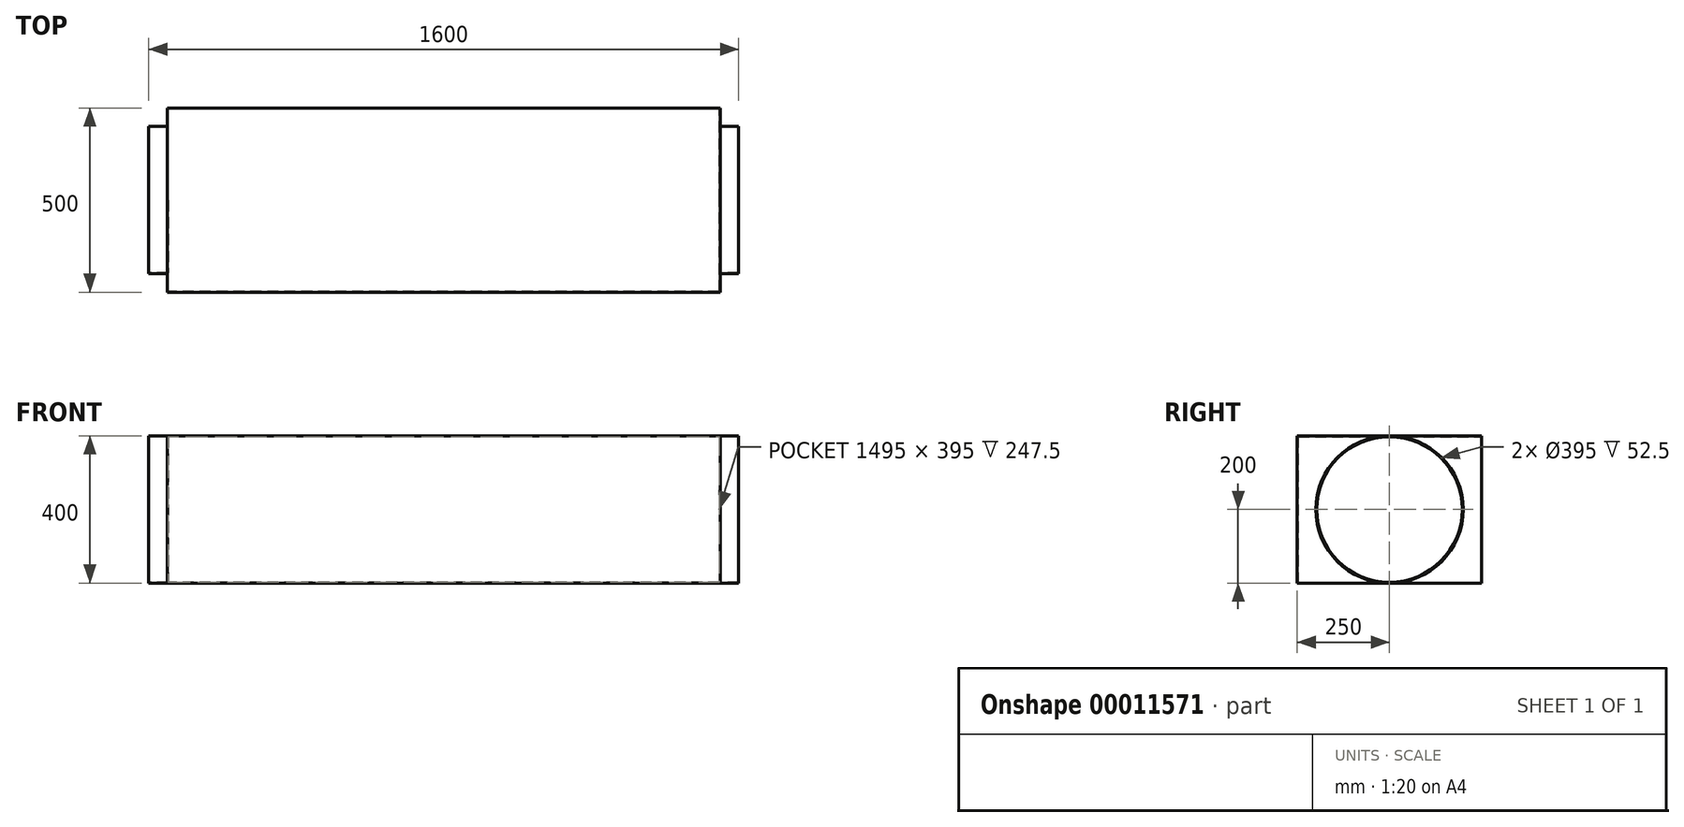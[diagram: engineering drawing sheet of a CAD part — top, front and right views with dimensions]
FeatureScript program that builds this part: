
annotation { "Feature Type Name" : "Feature", "Feature Type Description" : "" }
export const myFeature = defineFeature(function(context is Context, id is Id, definition is map)
    precondition{}
    {
        {
            var Q0;
            Q0=qCreatedBy(makeId("Right.planeOp"),FACE);
            var sketch = newSketch(context, id + "F0", { "sketchPlane" : qUnion([Q0])});
            skLineSegment(sketch, "E0.rect.bottom", {"start": v(-250, 200) * mm, "end": v(250, 200) * mm});
            skLineSegment(sketch, "E0.rect.top", {"start": v(-250, -200) * mm, "end": v(250, -200) * mm});
            skLineSegment(sketch, "E0.rect.left", {"start": v(-250, 200) * mm, "end": v(-250, -200) * mm});
            skLineSegment(sketch, "E0.rect.right", {"start": v(250, 200) * mm, "end": v(250, -200) * mm});
            skPoint(sketch, "E0.rect.middle", {"position": v(0, 0) * mm});
            skSolve(sketch);
        }
        {
            var Q0;
            Q0=makeQuery(id+"F0.imprint","IMPRINT",FACE,{"disambiguationData":[TD([[makeQuery(id+"F0.imprint","IMPRINT",EDGE,{"derivedFrom":sQuery(id+"F0.wireOp",EDGE,"E0.rect.bottom")}),-1.0]])]});
            extrude(context, id + "F1", {"entities" : qUnion([Q0]), "endBound" : BoundingType.SYMMETRIC, "depth" : 1500 * mm});
        }
        {
            var Q0;
            Q0=qCreatedBy(makeId("Right.planeOp"),FACE);
            var sketch = newSketch(context, id + "F2", { "sketchPlane" : qUnion([Q0])});
            skCircle(sketch, "E1", {"center": v(0, 0) * mm, "radius": 200 * mm});
            skSolve(sketch);
        }
        {
            var Q0;
            Q0 = qSketchRegion(id + "F2", true);
            extrude(context, id + "F3", {"entities" : qUnion([Q0]), "operationType" : NewBodyOperationType.ADD, "endBound" : BoundingType.SYMMETRIC, "depth" : 1600 * mm});
        }
        {
            var Q0;
            Q0=makeQuery(id+"F3.opExtrude","CAP_FACE",FACE,{"disambiguationData":[OSD([sQuery(id+"F2.wireOp",EDGE,"E1")])],"isStart":false});
            var Q1;
            Q1=makeQuery(id+"F3.opExtrude","CAP_FACE",FACE,{"disambiguationData":[OSD([sQuery(id+"F2.wireOp",EDGE,"E1")])],"isStart":true});
            shell(context, id + "F4", {"entities" : qUnion([Q0, Q1]), "thickness" : 2.5 * mm});
        }
    });
